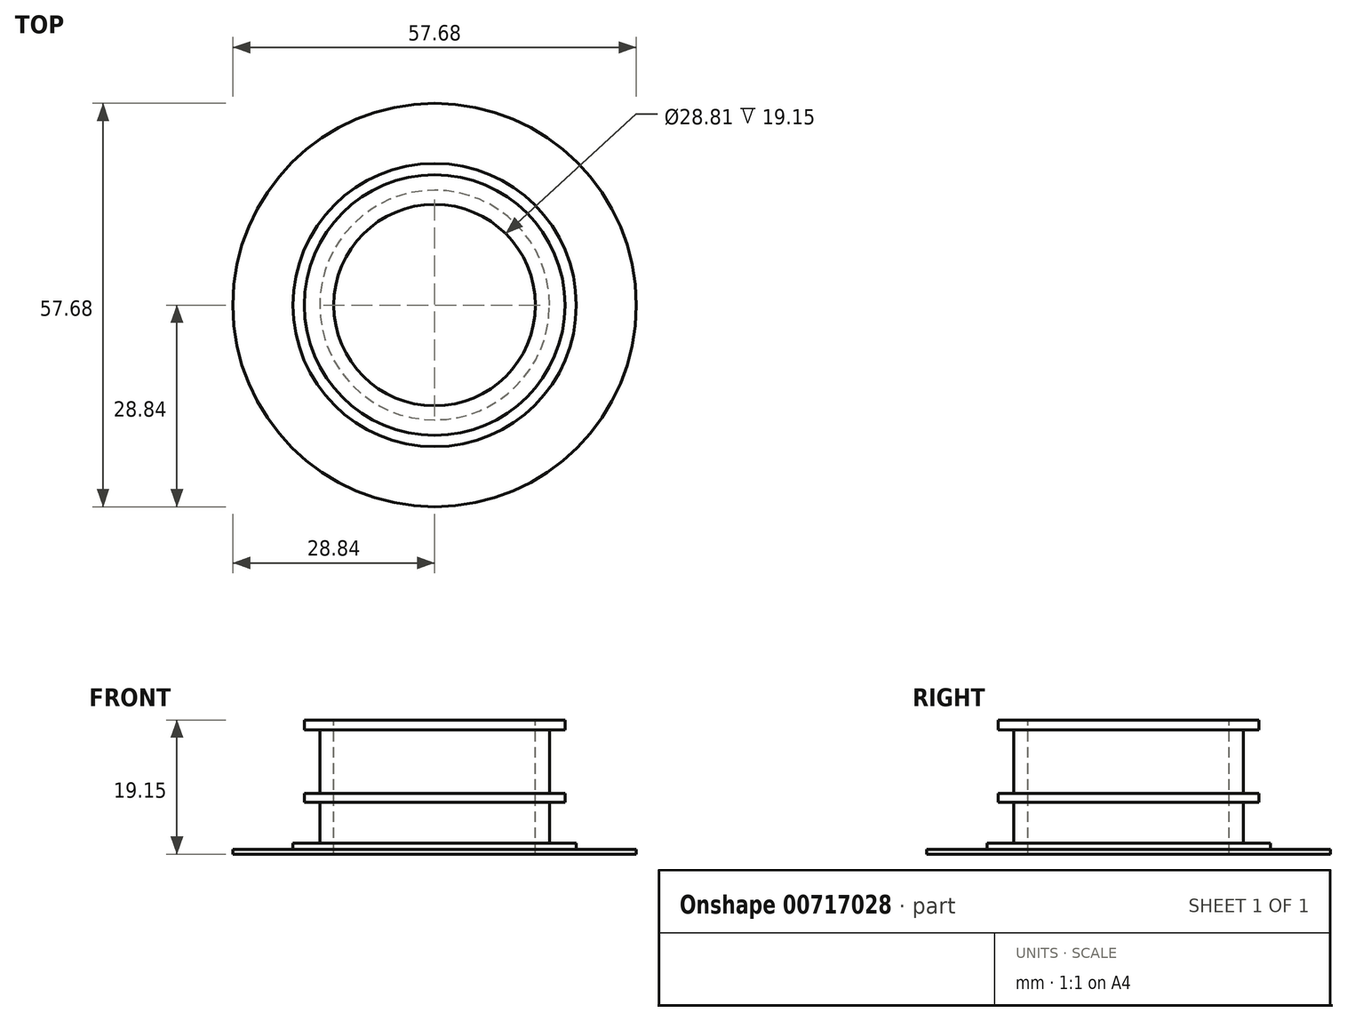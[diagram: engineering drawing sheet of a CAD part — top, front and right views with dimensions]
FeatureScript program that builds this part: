
annotation { "Feature Type Name" : "Feature", "Feature Type Description" : "" }
export const myFeature = defineFeature(function(context is Context, id is Id, definition is map)
    precondition{}
    {
        {
            var Q0;
            Q0=qCreatedBy(makeId("Right.planeOp"),FACE);
            var sketch = newSketch(context, id + "F0", { "sketchPlane" : qUnion([Q0])});
            skLineSegment(sketch, "E0", {"start": v(0, -19.15) * mm, "end": v(28.84, -19.15) * mm});
            skLineSegment(sketch, "E1", {"start": v(28.84, -19.15) * mm, "end": v(28.84, -18.46) * mm});
            skLineSegment(sketch, "E2", {"start": v(28.84, -18.46) * mm, "end": v(20.25, -18.46) * mm});
            skLineSegment(sketch, "E3", {"start": v(20.25, -18.46) * mm, "end": v(20.25, -17.56) * mm});
            skLineSegment(sketch, "E4", {"start": v(20.25, -17.56) * mm, "end": v(16.42, -17.56) * mm});
            skLineSegment(sketch, "E5", {"start": v(16.42, -17.56) * mm, "end": v(16.42, -11.75) * mm});
            skLineSegment(sketch, "E6", {"start": v(16.42, -11.75) * mm, "end": v(18.63, -11.75) * mm});
            skLineSegment(sketch, "E7", {"start": v(18.63, -11.75) * mm, "end": v(18.63, -10.48) * mm});
            skLineSegment(sketch, "E8", {"start": v(18.63, -10.48) * mm, "end": v(16.42, -10.48) * mm});
            skLineSegment(sketch, "E9", {"start": v(16.42, -10.48) * mm, "end": v(16.42, -1.4) * mm});
            skLineSegment(sketch, "E10", {"start": v(16.42, -1.4) * mm, "end": v(18.63, -1.4) * mm});
            skLineSegment(sketch, "E11", {"start": v(18.63, -1.4) * mm, "end": v(18.63, 0) * mm});
            skLineSegment(sketch, "E12", {"start": v(18.63, 0) * mm, "end": v(0, 0) * mm});
            skLineSegment(sketch, "E13", {"start": v(0, 0) * mm, "end": v(0, -19.15) * mm});
            skSolve(sketch);
        }
        {
            var Q0;
            Q0=makeQuery(id+"F0.imprint","IMPRINT",FACE,{"disambiguationData":[TD([[makeQuery(id+"F0.imprint","IMPRINT",EDGE,{"derivedFrom":sQuery(id+"F0.wireOp",EDGE,"E0")}),1.0]])]});
            var Q1;
            Q1=sQuery(id+"F0.wireOp",EDGE,"E13");
            revolve(context, id + "F1", {"surfaceOperationType" : NewSurfaceOperationType.NEW, "entities" : qUnion([Q0]), "axis" : qUnion([Q1]), "revolveType" : RevolveType.FULL});
        }
        {
            var Q0;
            Q0=makeQuery(id+"F1.opRevolve","SWEPT_FACE",FACE,{"disambiguationData":[OSD([sQuery(id+"F0.wireOp",EDGE,"E12")])]});
            var sketch = newSketch(context, id + "F2", { "sketchPlane" : qUnion([Q0])});
            skCircle(sketch, "E14", {"center": v(0, 0) * mm, "radius": 14.4 * mm});
            skSolve(sketch);
        }
        {
            var Q0;
            Q0=makeQuery(id+"F2.imprint","IMPRINT",FACE,{"disambiguationData":[TD([[makeQuery(id+"F2.imprint","IMPRINT",EDGE,{"derivedFrom":sQuery(id+"F2.wireOp",EDGE,"E14")}),1.0]])]});
            extrude(context, id + "F3", {"entities" : qUnion([Q0]), "operationType" : NewBodyOperationType.REMOVE, "endBound" : BoundingType.THROUGH_ALL, "oppositeDirection" : true, "depth" : 25 * mm, "offsetDistance" : 25 * mm});
        }
    });
